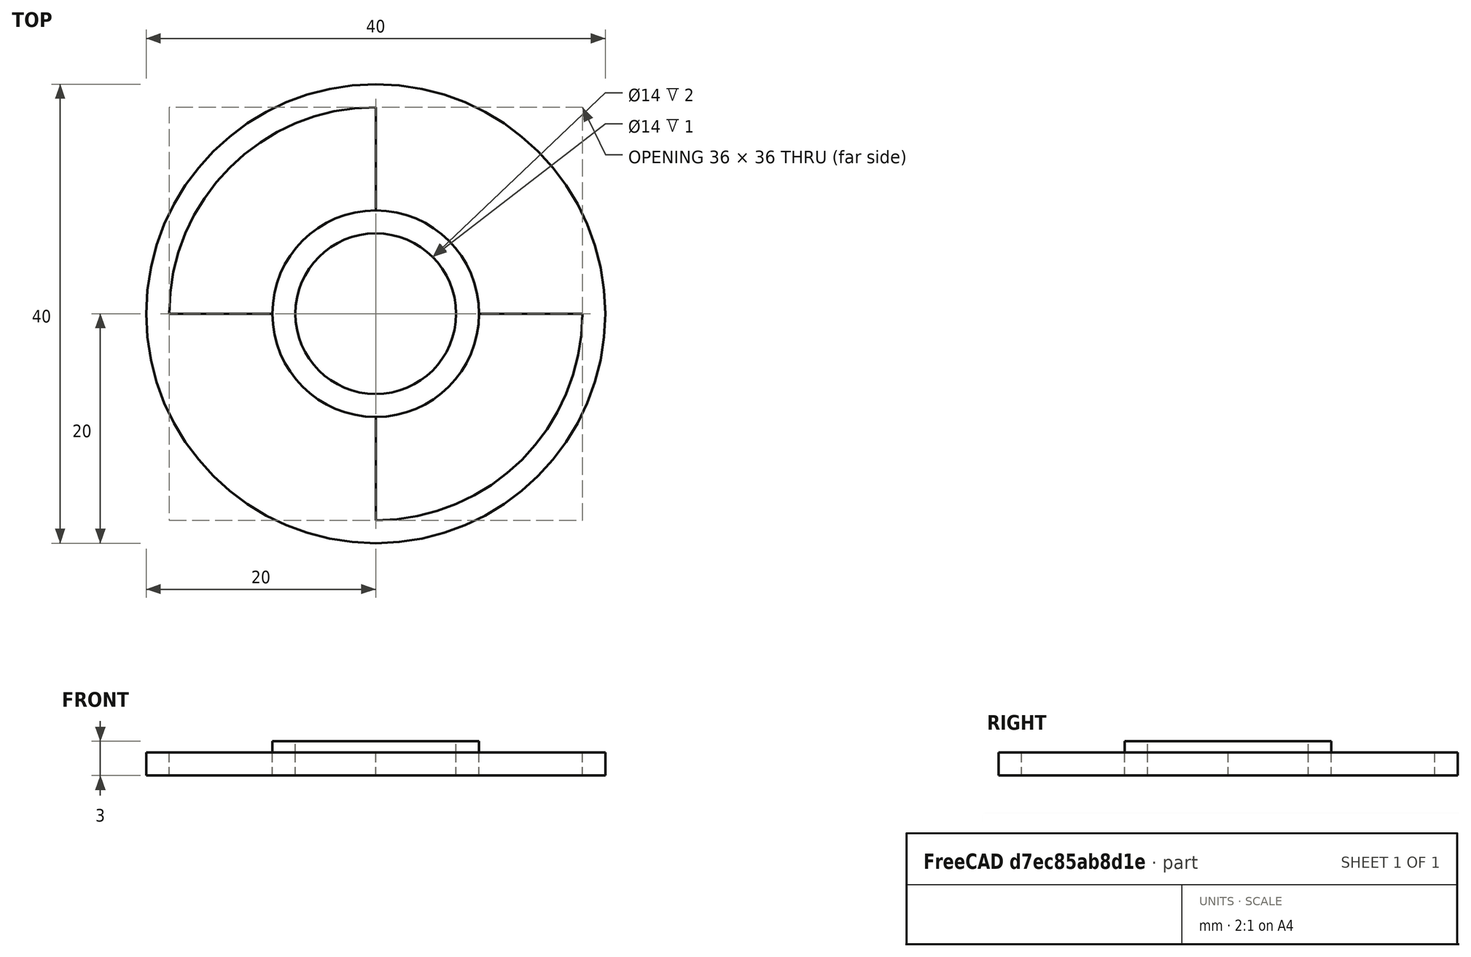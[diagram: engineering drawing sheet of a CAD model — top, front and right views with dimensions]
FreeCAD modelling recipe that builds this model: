
FCSTD DOCUMENT  (FreeCAD 0.19R24291 (Git))
Label: encodercito
License: All rights reserved
LicenseURL: http://en.wikipedia.org/wiki/All_rights_reserved
objects: Part::FeaturePython×3, Part::Cut×3, Part::Box×2, Part::MultiFuse×1
note: 9 computed .brp shape members not serialized (recipe doc carries the construction recipe); baked Part::Feature solids carry a one-line shape summary decoded from their .brp

FEATURE [Part::Box] Box  label="Cubo"
  AttacherType = Attacher::AttachEngine3D
  Height = 10
  Length = 20
  Width = 20
FEATURE [Part::Box] Box001  label="Cubo001"
  AttacherType = Attacher::AttachEngine3D
  Height = 10
  Length = 20
  Placement = pos=(-20,-20,0) rot=(0,0,1;0rad)
  Width = 20
FEATURE [Part::FeaturePython] Tube001  # WARN: FeaturePython — macro-defined, semantics opaque (R4)
  AttacherType = Attacher::AttachEngine3D
  Height = 2
  InnerRadius = 7
  OuterRadius = 20
FEATURE [Part::FeaturePython] Tube  # WARN: FeaturePython — macro-defined, semantics opaque (R4)
  AttacherType = Attacher::AttachEngine3D
  Height = 10
  InnerRadius = 9
  OuterRadius = 18
FEATURE [Part::Cut] Cut
  Base = -> Tube
  Tool = -> Box
FEATURE [Part::Cut] Cut001
  Base = -> Cut
  Tool = -> Box001
FEATURE [Part::Cut] Cut002
  Base = -> Tube001
  Tool = -> Cut001
FEATURE [Part::FeaturePython] Tube002  # WARN: FeaturePython — macro-defined, semantics opaque (R4)
  AttacherType = Attacher::AttachEngine3D
  Height = 3
  InnerRadius = 7
  OuterRadius = 9
FEATURE [Part::MultiFuse] Fusion
  Shapes = -> [Cut002,Tube002]
